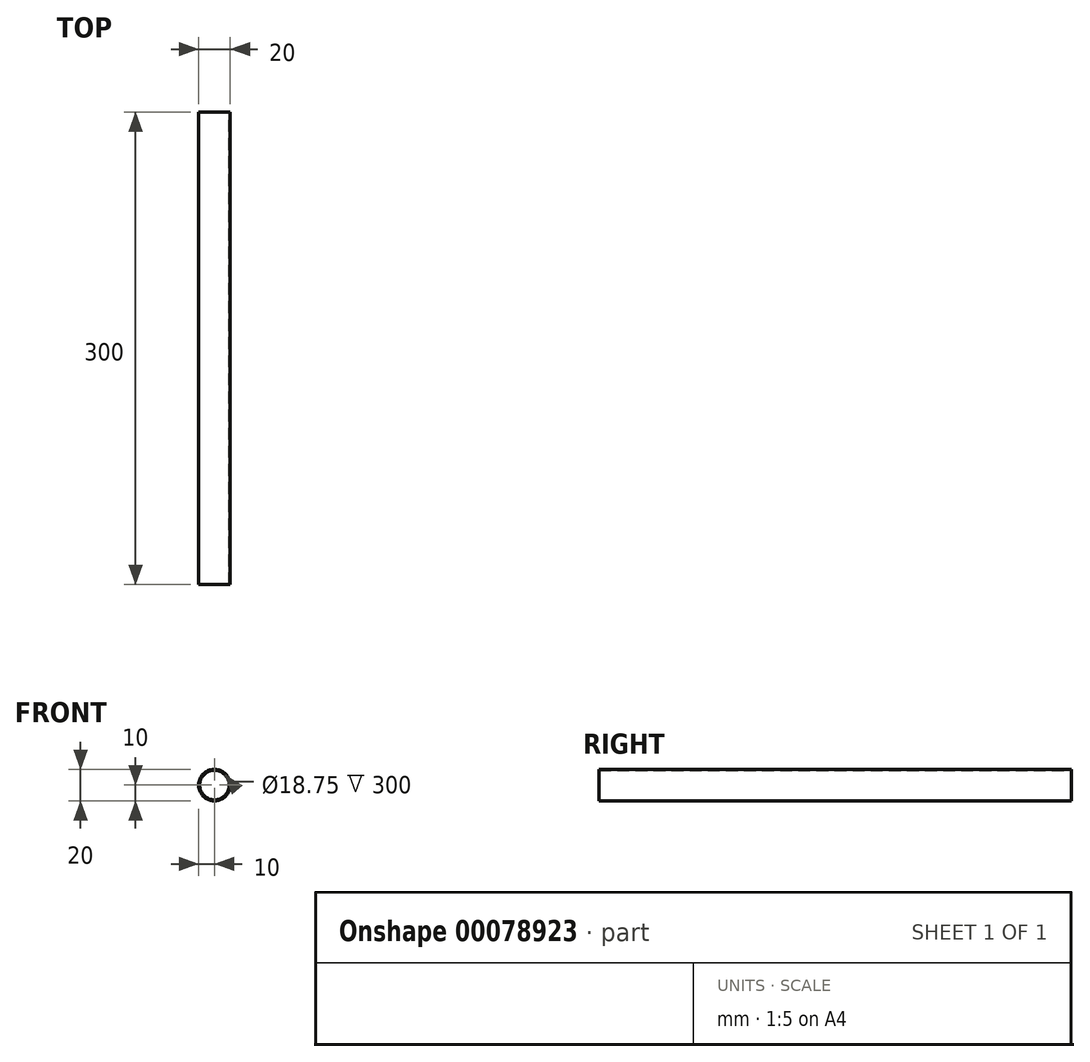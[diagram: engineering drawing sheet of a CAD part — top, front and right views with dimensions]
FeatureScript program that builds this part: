
annotation { "Feature Type Name" : "Feature", "Feature Type Description" : "" }
export const myFeature = defineFeature(function(context is Context, id is Id, definition is map)
    precondition{}
    {
        {
            var Q0;
            Q0=qCreatedBy(makeId("Front.planeOp"),FACE);
            var sketch = newSketch(context, id + "F1", { "sketchPlane" : qUnion([Q0])});
            skCircle(sketch, "E0", {"center": v(0, 0) * mm, "radius": 10 * mm});
            skCircle(sketch, "E1", {"center": v(0, 0) * mm, "radius": 9.38 * mm});
            skSolve(sketch);
        }
        {
            var Q0;
            Q0=qSketchRegion(id+"F1",true);
            extrude(context, id + "F0", {"entities" : qUnion([Q0]), "depth" : 300 * mm});
        }
    });
